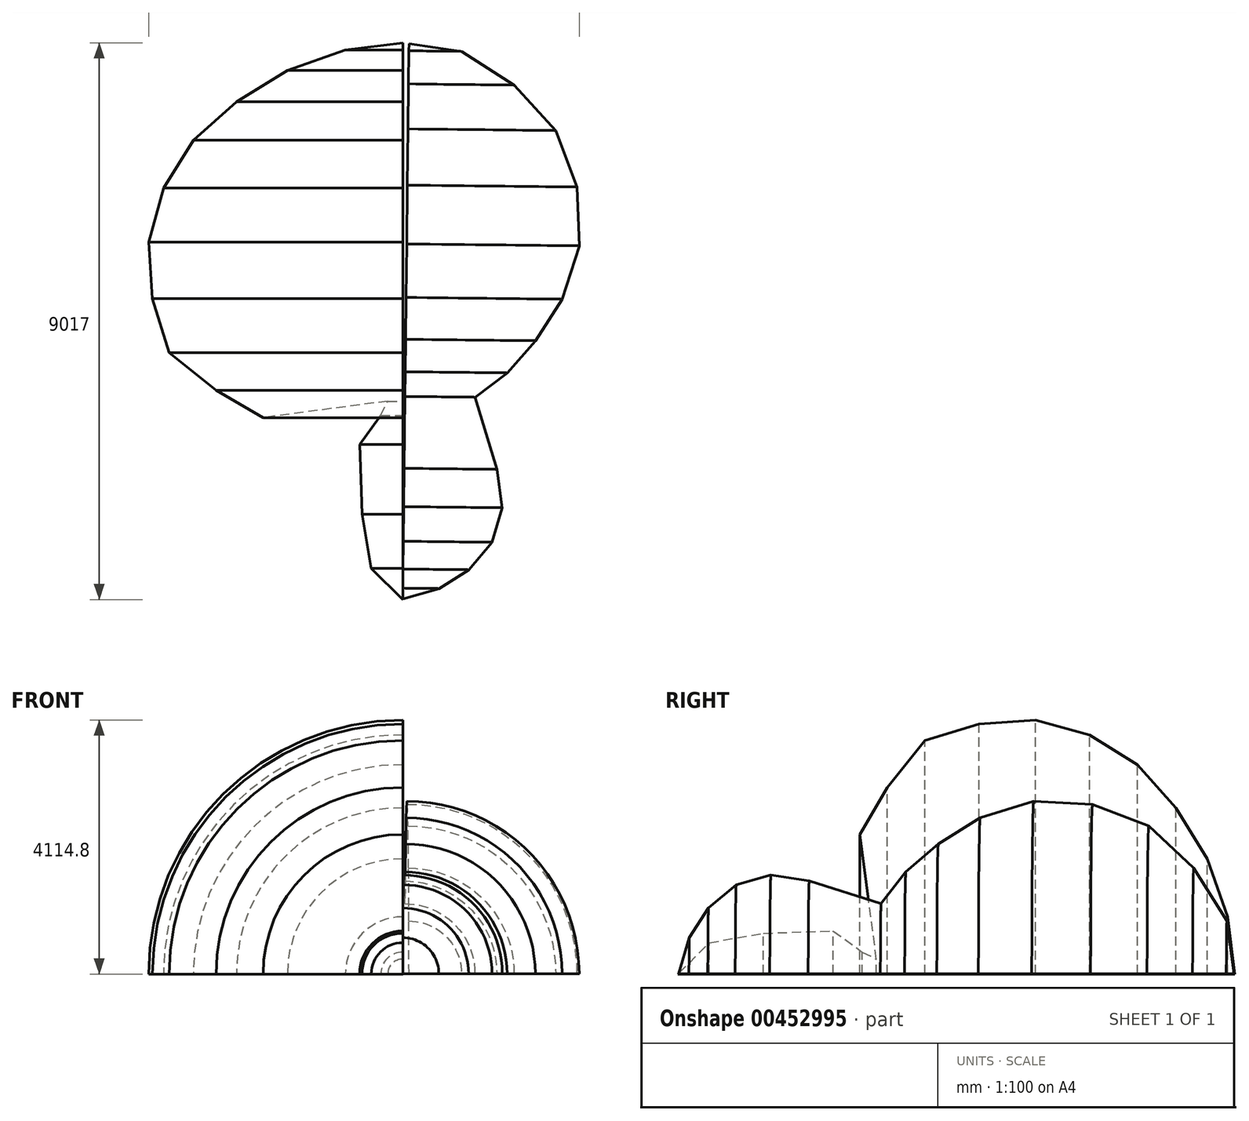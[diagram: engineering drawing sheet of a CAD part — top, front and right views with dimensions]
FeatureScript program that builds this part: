
annotation { "Feature Type Name" : "Feature", "Feature Type Description" : "" }
export const myFeature = defineFeature(function(context is Context, id is Id, definition is map)
    precondition{}
    {
        {
            var Q0;
            Q0=qCreatedBy(makeId("Top.planeOp"),FACE);
            var sketch = newSketch(context, id + "F0", { "sketchPlane" : qUnion([Q0])});
            skLineSegment(sketch, "E0", {"start": v(101.6, 4495.8) * mm, "end": v(952.5, 4368.8) * mm});
            skLineSegment(sketch, "E1", {"start": v(952.5, 4368.8) * mm, "end": v(1803.4, 3822.7) * mm});
            skLineSegment(sketch, "E2", {"start": v(1803.4, 3822.7) * mm, "end": v(2476.5, 3086.1) * mm});
            skLineSegment(sketch, "E3", {"start": v(2476.5, 3086.1) * mm, "end": v(2819.4, 2171.7) * mm});
            skLineSegment(sketch, "E4", {"start": v(2819.4, 2171.7) * mm, "end": v(2857.5, 1219.2) * mm});
            skLineSegment(sketch, "E5", {"start": v(2857.5, 1219.2) * mm, "end": v(2578.1, 355.6) * mm});
            skLineSegment(sketch, "E6", {"start": v(2578.1, 355.6) * mm, "end": v(2146.3, -317.5) * mm});
            skLineSegment(sketch, "E7", {"start": v(2146.3, -317.5) * mm, "end": v(1689.1, -838.2) * mm});
            skLineSegment(sketch, "E8", {"start": v(1689.1, -838.2) * mm, "end": v(1168.4, -1231.9) * mm});
            skLineSegment(sketch, "E9", {"start": v(1168.4, -1231.9) * mm, "end": v(1524, -2400.3) * mm});
            skLineSegment(sketch, "E10", {"start": v(1524, -2400.3) * mm, "end": v(1612.9, -3022.6) * mm});
            skLineSegment(sketch, "E11", {"start": v(1612.9, -3022.6) * mm, "end": v(1447.8, -3581.4) * mm});
            skLineSegment(sketch, "E12", {"start": v(1447.8, -3581.4) * mm, "end": v(1066.8, -4025.9) * mm});
            skLineSegment(sketch, "E13", {"start": v(1066.8, -4025.9) * mm, "end": v(584.2, -4330.7) * mm});
            skLineSegment(sketch, "E14", {"start": v(584.2, -4330.7) * mm, "end": v(0, -4495.8) * mm});
            skLineSegment(sketch, "E15", {"start": v(101.6, 4495.8) * mm, "end": v(0, -4495.8) * mm});
            skSolve(sketch);
        }
        {
            var Q0;
            Q0=qCreatedBy(makeId("Right.planeOp"),FACE);
            var sketch = newSketch(context, id + "F1", { "sketchPlane" : qUnion([Q0])});
            skLineSegment(sketch, "E16", {"start": v(-508, 3778.25) * mm, "end": v(368.3, 4044.95) * mm});
            skLineSegment(sketch, "E17", {"start": v(368.3, 4044.95) * mm, "end": v(1282.7, 4108.45) * mm});
            skLineSegment(sketch, "E18", {"start": v(1282.7, 4108.45) * mm, "end": v(2159, 3867.15) * mm});
            skLineSegment(sketch, "E19", {"start": v(2159, 3867.15) * mm, "end": v(2933.7, 3384.55) * mm});
            skLineSegment(sketch, "E20", {"start": v(2933.7, 3384.55) * mm, "end": v(3556, 2686.05) * mm});
            skLineSegment(sketch, "E21", {"start": v(3556, 2686.05) * mm, "end": v(4064, 1860.55) * mm});
            skLineSegment(sketch, "E22", {"start": v(4064, 1860.55) * mm, "end": v(4394.2, 920.75) * mm});
            skLineSegment(sketch, "E23", {"start": v(4394.2, 920.75) * mm, "end": v(4508.5, -6.35) * mm});
            skLineSegment(sketch, "E24", {"start": v(-4508.5, -6.35) * mm, "end": v(-4000.5, 501.65) * mm});
            skLineSegment(sketch, "E25", {"start": v(-4000.5, 501.65) * mm, "end": v(-3124.2, 654.05) * mm});
            skLineSegment(sketch, "E26", {"start": v(-3124.2, 654.05) * mm, "end": v(-1993.9, 692.15) * mm});
            skLineSegment(sketch, "E27", {"start": v(-1993.9, 692.15) * mm, "end": v(-1524, 349.25) * mm});
            skLineSegment(sketch, "E28", {"start": v(-1524, 349.25) * mm, "end": v(-1295.4, 234.95) * mm});
            skLineSegment(sketch, "E29", {"start": v(-1295.4, 234.95) * mm, "end": v(-1562.1, 2254.25) * mm});
            skLineSegment(sketch, "E30", {"start": v(-1562.1, 2254.25) * mm, "end": v(-1117.6, 3016.25) * mm});
            skLineSegment(sketch, "E31", {"start": v(-1117.6, 3016.25) * mm, "end": v(-508, 3778.25) * mm});
            skLineSegment(sketch, "E32", {"start": v(4508.5, -6.35) * mm, "end": v(-4508.5, -6.35) * mm});
            skSolve(sketch);
        }
        {
            var Q0;
            Q0=makeQuery(id+"F0.imprint","IMPRINT",FACE,{"disambiguationData":[TD([[makeQuery(id+"F0.imprint","IMPRINT",EDGE,{"derivedFrom":sQuery(id+"F0.wireOp",EDGE,"E0")}),-1.0]])]});
            var Q1;
            Q1=sQuery(id+"F0.wireOp",EDGE,"E15");
            revolve(context, id + "F2", {"entities" : qUnion([Q0]), "axis" : qUnion([Q1]), "revolveType" : RevolveType.ONE_DIRECTION, "angle" : 90 * degree});
        }
        {
            var Q0;
            Q0=makeQuery(id+"F1.imprint","IMPRINT",FACE,{"disambiguationData":[TD([[makeQuery(id+"F1.imprint","IMPRINT",EDGE,{"derivedFrom":sQuery(id+"F1.wireOp",EDGE,"E16")}),-1.0]])]});
            var Q1;
            Q1=sQuery(id+"F1.wireOp",EDGE,"E32");
            revolve(context, id + "F3", {"entities" : qUnion([Q0]), "axis" : qUnion([Q1]), "revolveType" : RevolveType.ONE_DIRECTION, "angle" : 90 * degree});
        }
    });
